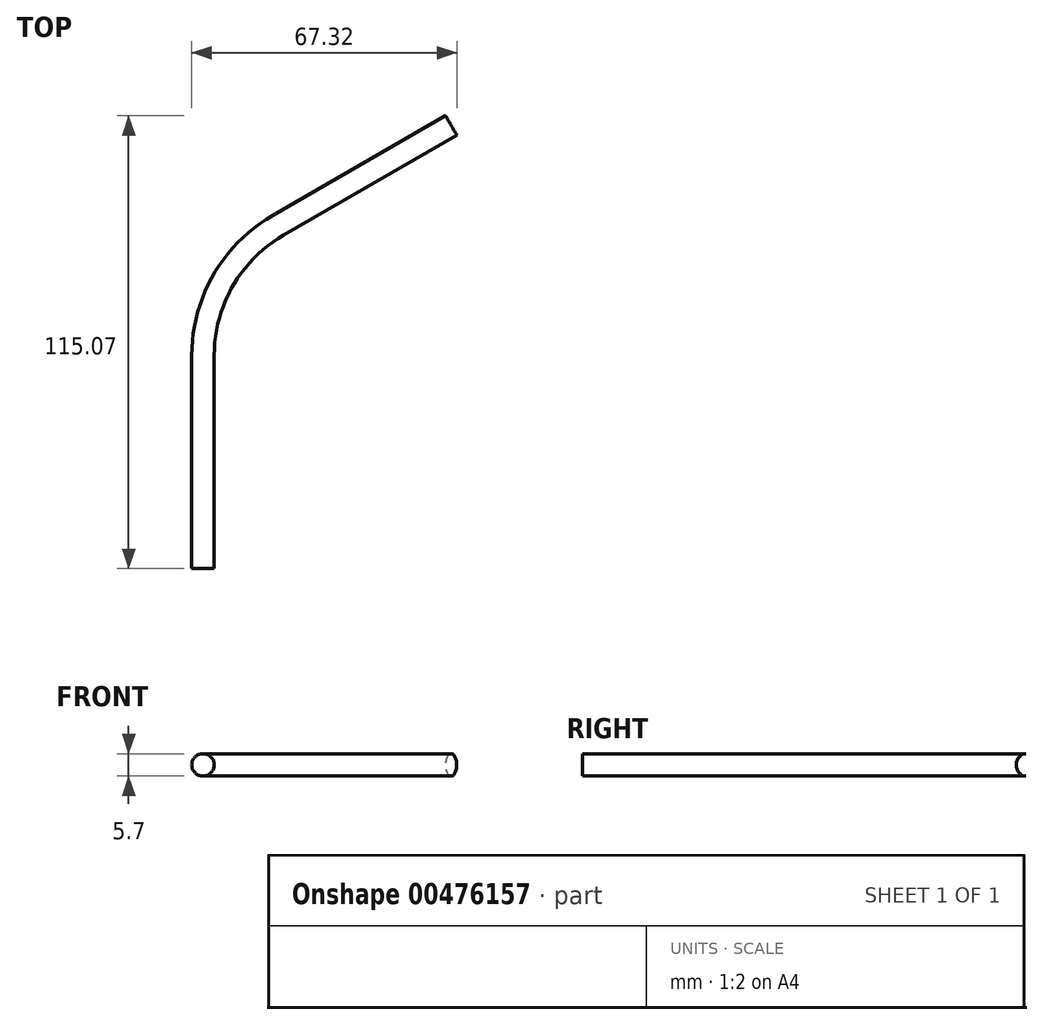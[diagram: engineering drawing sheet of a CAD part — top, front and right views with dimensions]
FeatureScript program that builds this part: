
annotation { "Feature Type Name" : "Feature", "Feature Type Description" : "" }
export const myFeature = defineFeature(function(context is Context, id is Id, definition is map)
    precondition{}
    {
        {
            var Q0;
            Q0=qCreatedBy(makeId("Top.planeOp"),FACE);
            var sketch = newSketch(context, id + "F0", { "sketchPlane" : qUnion([Q0])});
            skLineSegment(sketch, "E0", {"start": v(0, 0) * mm, "end": v(0, 16.1) * mm});
            skLineSegment(sketch, "E1", {"start": v(19.05, 49.1) * mm, "end": v(63.04, 74.5) * mm});
            skLineSegment(sketch, "E2", {"start": v(0, 0) * mm, "end": v(0, -38.1) * mm});
            skPoint(sketch, "E3.visualSharp", {"position": v(0, 38.1) * mm});
            skArc(sketch, "E3.filletArc", {"start": v(19.05, 49.1) * mm, "mid": v(5.1, 35.15) * mm, "end": v(0, 16.1) * mm});
            skPoint(sketch, "E4.visualSharp", {"position": v(175.98, 139.7) * mm});
            skSolve(sketch);
        }
        {
            var Q0;
            Q0=qCreatedBy(makeId("Front.planeOp"),FACE);
            var sketch = newSketch(context, id + "F1", { "sketchPlane" : qUnion([Q0])});
            skCircle(sketch, "E5", {"center": v(0, 0) * mm, "radius": 2.85 * mm});
            skSolve(sketch);
        }
        {
            var Q0;
            Q0=makeQuery(id+"F1.imprint","IMPRINT",FACE,{"disambiguationData":[TD([[makeQuery(id+"F1.imprint","IMPRINT",EDGE,{"derivedFrom":sQuery(id+"F1.wireOp",EDGE,"E5")}),1.0]])]});
            var Q1;
            Q1=sQuery(id+"F0.wireOp",EDGE,"E0");
            var Q2;
            Q2=sQuery(id+"F0.wireOp",EDGE,"E3.filletArc");
            var Q3;
            Q3=sQuery(id+"F0.wireOp",EDGE,"E1");
            var Q4;
            Q4=sQuery(id+"F0.wireOp",EDGE,"E4.filletArc");
            var Q5;
            Q5=sQuery(id+"F0.wireOp",EDGE,"lWv93iFz-bEN9-oXhL-jszu-YtIgDBo05eqF");
            var Q6;
            Q6=sQuery(id+"F0.wireOp",EDGE,"rNUARqjs-TsUK-Telz-jRy7-cFuhtV7gu0Rw");
            sweep(context, id + "F2", {"profiles" : qUnion([Q0]), "path" : qUnion([Q1, Q2, Q3, Q4, Q5, Q6])});
        }
        {
            var Q0;
            Q0=qSketchRegion(id+"F1",true);
            var Q1;
            Q1=sQuery(id+"F0.wireOp",EDGE,"E2");
            sweep(context, id + "F3", {"operationType" : NewBodyOperationType.ADD, "profiles" : qUnion([Q0]), "path" : qUnion([Q1])});
        }
    });
